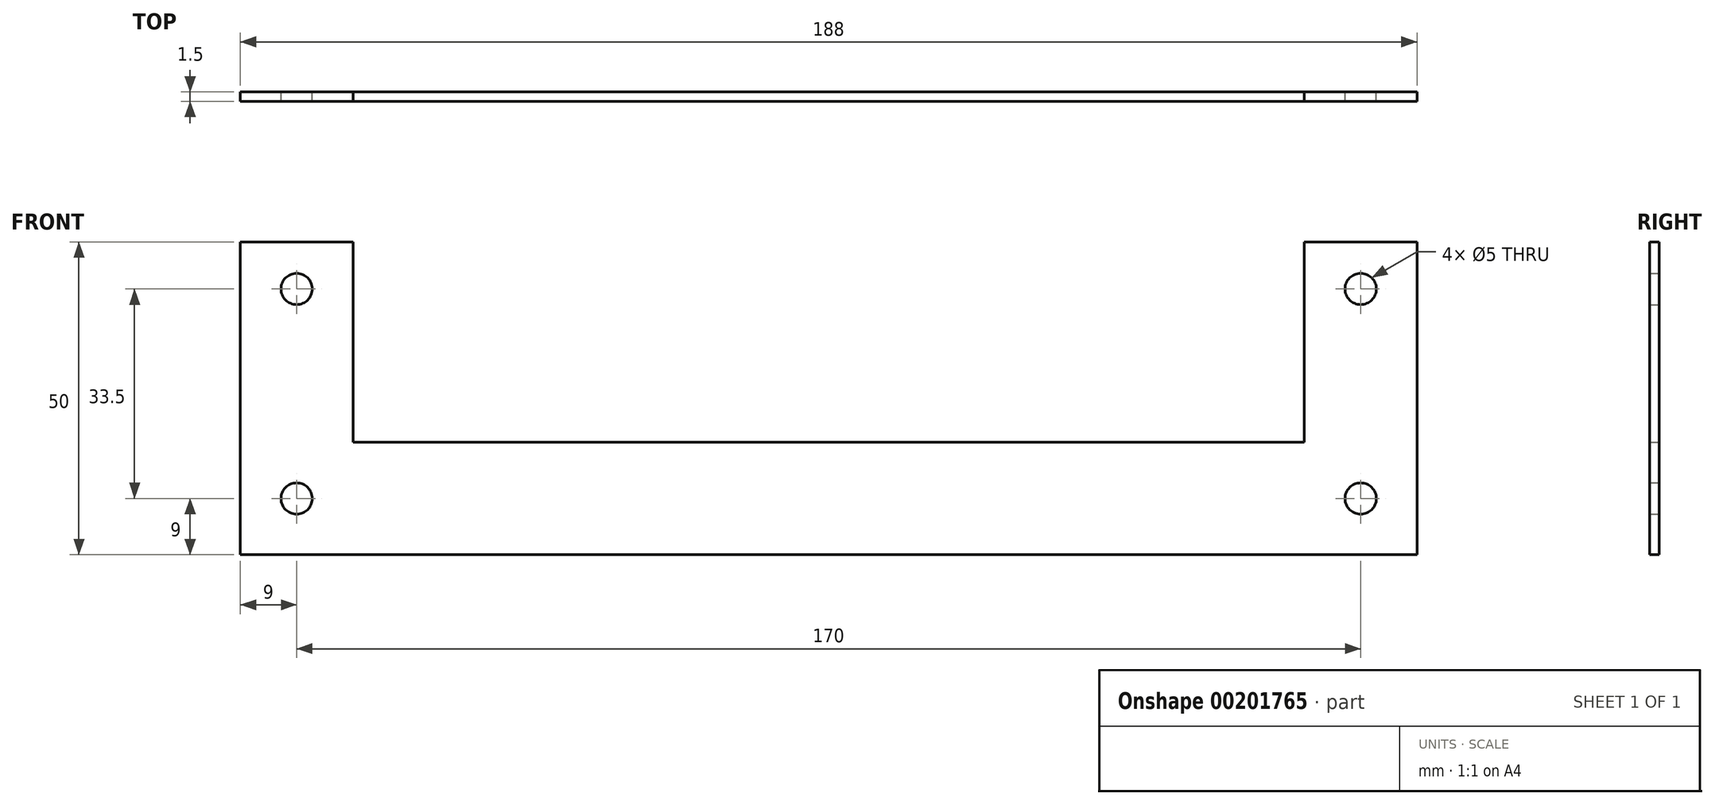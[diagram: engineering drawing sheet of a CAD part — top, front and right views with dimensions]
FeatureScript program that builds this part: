
annotation { "Feature Type Name" : "Feature", "Feature Type Description" : "" }
export const myFeature = defineFeature(function(context is Context, id is Id, definition is map)
    precondition{}
    {
        {
            var Q0;
            Q0=qCreatedBy(makeId("Front.planeOp"),FACE);
            var sketch = newSketch(context, id + "F0", { "sketchPlane" : qUnion([Q0])});
            skLineSegment(sketch, "E0", {"start": v(0, 0) * mm, "end": v(-94, 0) * mm});
            skLineSegment(sketch, "E1", {"start": v(-94, 0) * mm, "end": v(-94, 50) * mm});
            skLineSegment(sketch, "E2", {"start": v(-94, 50) * mm, "end": v(-76, 50) * mm});
            skLineSegment(sketch, "E3", {"start": v(-76, 50) * mm, "end": v(-76, 18) * mm});
            skLineSegment(sketch, "E4", {"start": v(-76, 18) * mm, "end": v(0, 18) * mm});
            skLineSegment(sketch, "E5", {"start": v(-85, 50) * mm, "end": v(-85, 0) * mm, "construction": true});
            skCircle(sketch, "E6", {"center": v(-85, 42.5) * mm, "radius": 2.5 * mm});
            skCircle(sketch, "E7", {"center": v(-85, 9) * mm, "radius": 2.5 * mm});
            skLineSegment(sketch, "E8", {"start": v(0, 0) * mm, "end": v(0, 31.13) * mm, "construction": true});
            skCircle(sketch, "E9.MirrorC", {"center": v(85, 42.5) * mm, "radius": 2.5 * mm});
            skCircle(sketch, "E10.MirrorC", {"center": v(85, 9) * mm, "radius": 2.5 * mm});
            skLineSegment(sketch, "E11.MirrorCS", {"start": v(76, 18) * mm, "end": v(0, 18) * mm});
            skLineSegment(sketch, "E12.MirrorCS", {"start": v(76, 50) * mm, "end": v(76, 18) * mm});
            skLineSegment(sketch, "E13.MirrorCS", {"start": v(85, 50) * mm, "end": v(85, 0) * mm, "construction": true});
            skLineSegment(sketch, "E14.MirrorCS", {"start": v(94, 0) * mm, "end": v(94, 50) * mm});
            skLineSegment(sketch, "E15.MirrorCS", {"start": v(94, 50) * mm, "end": v(76, 50) * mm});
            skLineSegment(sketch, "E16.MirrorCS", {"start": v(0, 0) * mm, "end": v(94, 0) * mm});
            skSolve(sketch);
        }
        {
            var Q0;
            Q0=makeQuery(id+"F0.imprint","IMPRINT",FACE,{"disambiguationData":[TD([[makeQuery(id+"F0.imprint","IMPRINT",EDGE,{"derivedFrom":sQuery(id+"F0.wireOp",EDGE,"E0")}),-1.0]])]});
            extrude(context, id + "F1", {"entities" : qUnion([Q0]), "depth" : 1.5 * mm, "offsetDistance" : 25 * mm});
        }
    });
